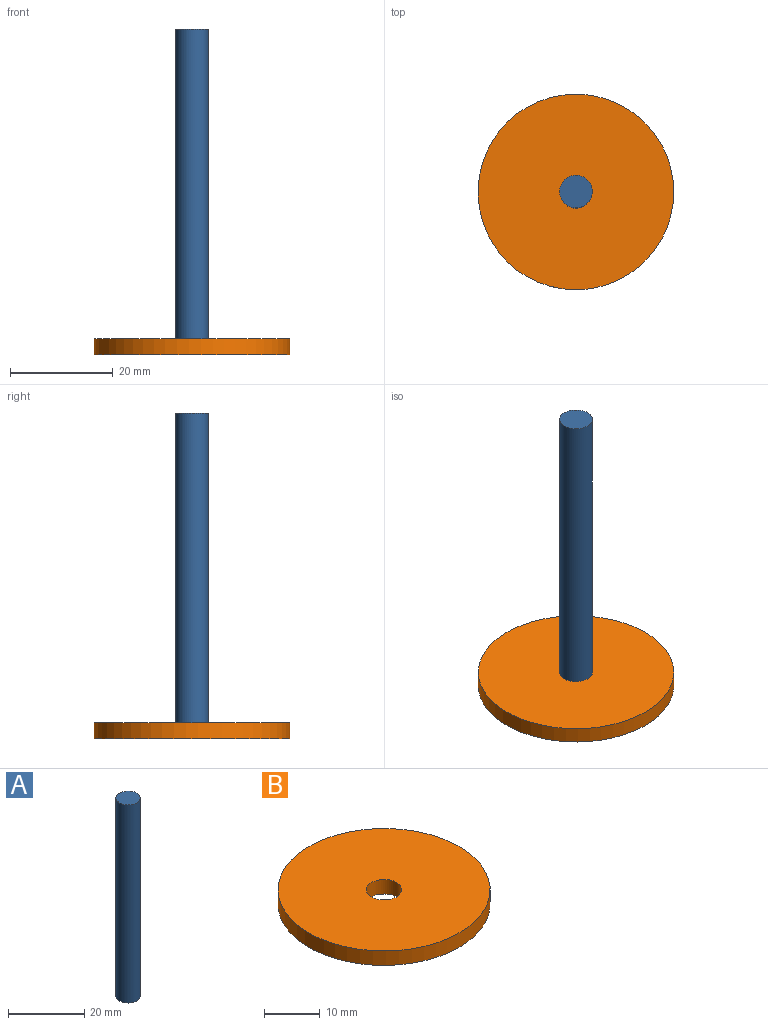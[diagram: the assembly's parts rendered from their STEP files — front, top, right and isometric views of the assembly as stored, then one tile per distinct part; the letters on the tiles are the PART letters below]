
ASSEMBLY  parts=2 mates=1
PART A: 3 faces, bbox 6.4x6.4x63.5 mm
  f0: plane 6.35x6.35mm, normal (0,0,1), area 31.7mm2, adj f1
  f1: cylinder r=3.17mm len=63.5mm, axis (0,0,-1), area 1266.8mm2, adj f0,f2
  f2: plane 6.35x6.35mm, normal (0,0,-1), area 31.7mm2, adj f1
PART B: 4 faces, bbox 38.1x38.1x3.2 mm
  f0: cylinder r=3.17mm len=6.35mm, axis (0,0,-1), area 63.3mm2, adj f2,f3
  f1: cylinder r=19.05mm len=38.1mm, axis (0,0,-1), area 380mm2, adj f2,f3
  f2: plane 38.1x38.1mm, normal (0,0,1), area 1108.4mm2, adj f0,f1
  f3: plane 38.1x38.1mm, normal (0,0,-1), area 1108.4mm2, adj f0,f1
PLACE A t=(-31.75,0,-69.85)mm
PLACE B t=(-31.75,0,-69.85)mm
MATE fastened B.f1 <-> A.f1  axis (0,0,-1) through (0,0,0)mm
